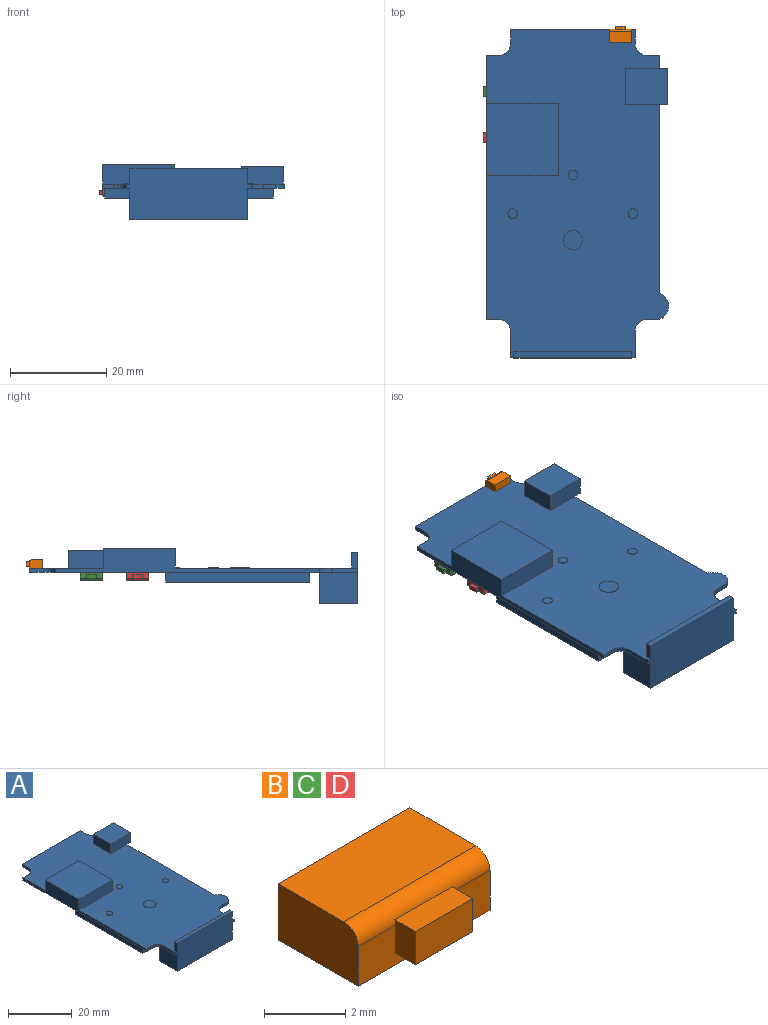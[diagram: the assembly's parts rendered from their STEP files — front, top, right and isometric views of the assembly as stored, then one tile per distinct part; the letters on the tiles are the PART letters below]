
ASSEMBLY  parts=4 mates=3
PART A: 54 faces, bbox 37.9x68.3x11.5 mm
  f0: plane 68.3x37.9mm, normal (0,0,1), area 2001.6mm2, adj f2,f3,f4,f5,f6,f7,f8,f9
  f1: plane 68.3x37.9mm, normal (0,0,-1), area 1085.4mm2, adj f2,f3,f4,f5,f6,f7,f8,f9
  f2: plane 49.4x0.9mm, normal (1,0,0), area 44.5mm2, adj f0,f1,f3,f18,f28
  f3: plane 2.5x0.9mm, normal (0,1,0), area 2.3mm2, adj f0,f1,f2,f4
  f4: cylinder r=2.5mm len=2.5mm, axis (0,0,-1), area 3.5mm2, adj f0,f1,f3,f5
  f5: plane 2.9x0.9mm, normal (1,0,0), area 2.6mm2, adj f0,f1,f4,f6
  f6: plane 25.9x0.9mm, normal (0,1,0), area 23.3mm2, adj f0,f1,f5,f7
  f7: plane 2.9x0.9mm, normal (-1,0,0), area 2.6mm2, adj f0,f1,f6,f8
  f8: cylinder r=2.5mm len=2.5mm, axis (0,0,-1), area 3.5mm2, adj f0,f1,f7,f9
  f9: plane 2.5x0.9mm, normal (0,1,0), area 2.3mm2, adj f0,f1,f8,f10
  f10: plane 54.9x5mm, normal (-1,0,0), area 110.5mm2, adj f0,f1,f9,f11,f19,f20,f22
  f11: plane 2.5x0.9mm, normal (0,-1,0), area 2.3mm2, adj f0,f1,f10,f12
  f12: cylinder r=2.5mm len=2.5mm, axis (0,0,-1), area 3.5mm2, adj f0,f1,f11,f13
  f13: plane 5.5x0.9mm, normal (-1,0,0), area 5mm2, adj f0,f1,f12,f14
  f14: plane 25.9x10.7mm, normal (0,-1,0), area 263.4mm2, adj f0,f1,f13,f15,f29,f31,f34,f46
  f15: plane 5.5x0.9mm, normal (1,0,0), area 5mm2, adj f0,f1,f14,f16
  f16: cylinder r=2.5mm len=2.5mm, axis (0,0,-1), area 3.5mm2, adj f0,f1,f15,f17
  f17: plane 2.5x0.9mm, normal (0,-1,0), area 2.3mm2, adj f0,f1,f16,f18
  f18: cylinder r=2.89mm len=5.5mm, axis (0,0,-1), area 6.5mm2, adj f0,f1,f2,f17
  f19: plane 14.9x4.1mm, normal (0,1,0), area 61.1mm2, adj f0,f10,f21,f22
  f20: plane 14.9x4.1mm, normal (0,-1,0), area 61.1mm2, adj f0,f10,f21,f22
  f21: plane 14.9x4.1mm, normal (1,0,0), area 61.1mm2, adj f0,f19,f20,f22
  f22: plane 14.9x14.9mm, normal (0,0,1), area 222mm2, adj f10,f19,f20,f21
  f23: plane 8.8x3.7mm, normal (0,1,0), area 32.6mm2, adj f0,f24,f26,f27,f28
  f24: plane 7.6x3.7mm, normal (-1,0,0), area 28.1mm2, adj f0,f23,f25,f27
  f25: plane 8.8x3.7mm, normal (0,-1,0), area 32.6mm2, adj f0,f24,f26,f27,f28
  f26: plane 7.6x3.7mm, normal (1,0,0), area 28.1mm2, adj f23,f25,f27,f28
  f27: plane 8.8x7.6mm, normal (0,0,1), area 66.9mm2, adj f23,f24,f25,f26
  f28: plane 7.6x1.7mm, normal (0,0,-1), area 12.9mm2, adj f2,f23,f25,f26
  f29: plane 8x6.5mm, normal (1,0,0), area 52mm2, adj f1,f14,f30,f34
  f30: plane 24.5x6.5mm, normal (0,1,0), area 159.3mm2, adj f1,f29,f31,f34
  f31: plane 8x6.5mm, normal (-1,0,0), area 52mm2, adj f1,f14,f30,f34
  f32: cylinder r=1mm len=6.5mm, axis (0,0,1), area 40.8mm2, adj f34,f36
  f33: cylinder r=1mm len=6.5mm, axis (0,0,1), area 40.8mm2, adj f34,f35
  f34: plane 24.5x8mm, normal (0,0,-1), area 189.7mm2, adj f14,f29,f30,f31,f32,f33
  f35: plane 2x2mm, normal (0,0,-1), area 3.1mm2, adj f33
  f36: plane 2x2mm, normal (0,0,-1), area 3.1mm2, adj f32
  f37: cylinder r=2mm len=4mm, axis (0,0,-1), area 1.3mm2, adj f0,f38
  f38: plane 4x4mm, normal (0,0,1), area 12.6mm2, adj f37
  f39: cylinder r=1mm len=2mm, axis (0,0,-1), area 0.6mm2, adj f0,f40
  f40: plane 2x2mm, normal (0,0,1), area 3.1mm2, adj f39
  f41: cylinder r=1mm len=2mm, axis (0,0,-1), area 0.6mm2, adj f0,f42
  f42: plane 2x2mm, normal (0,0,1), area 3.1mm2, adj f41
  f43: cylinder r=1mm len=2mm, axis (0,0,-1), area 0.6mm2, adj f0,f44
  f44: plane 2x2mm, normal (0,0,1), area 3.1mm2, adj f43
  f45: plane 24.5x3.3mm, normal (0,1,0), area 80.9mm2, adj f0,f46,f47,f48
  f46: plane 3.3x1.3mm, normal (-1,0,0), area 4.3mm2, adj f0,f14,f45,f48
  f47: plane 3.3x1.3mm, normal (1,0,0), area 4.3mm2, adj f0,f14,f45,f48
  f48: plane 24.5x1.3mm, normal (0,0,1), area 31.9mm2, adj f14,f45,f46,f47
  f49: plane 35x2mm, normal (0,-1,0), area 70mm2, adj f1,f50,f52,f53
  f50: plane 30x2mm, normal (-1,0,0), area 60mm2, adj f1,f49,f51,f53
  f51: plane 35x2mm, normal (0,1,0), area 70mm2, adj f1,f50,f52,f53
  f52: plane 30x2mm, normal (1,0,0), area 60mm2, adj f1,f49,f51,f53
  f53: plane 35x30mm, normal (0,0,-1), area 1050mm2, adj f49,f50,f51,f52
PART B: 12 faces, bbox 4.6x3.5x1.7 mm
  f0: plane 4.6x1.2mm, normal (0,-1,0), area 3.8mm2, adj f1,f3,f5,f6,f8,f9,f11
  f1: plane 2.8x1.7mm, normal (1,0,0), area 4.7mm2, adj f0,f2,f4,f5,f11
  f2: plane 4.6x1.7mm, normal (0,1,0), area 7.8mm2, adj f1,f3,f4,f5
  f3: plane 2.8x1.7mm, normal (-1,0,0), area 4.7mm2, adj f0,f2,f4,f5,f11
  f4: plane 4.6x2.3mm, normal (0,0,1), area 10.6mm2, adj f1,f2,f3,f11
  f5: plane 4.6x2.8mm, normal (0,0,-1), area 12.9mm2, adj f0,f1,f2,f3
  f6: plane 1x0.72mm, normal (1,0,0), area 0.7mm2, adj f0,f7,f9,f10,f11
  f7: plane 2x0.72mm, normal (0,0,1), area 1.4mm2, adj f6,f8,f10,f11
  f8: plane 1x0.72mm, normal (-1,0,0), area 0.7mm2, adj f0,f7,f9,f10,f11
  f9: plane 2x0.7mm, normal (0,0,-1), area 1.4mm2, adj f0,f6,f8,f10
  f10: plane 2x1mm, normal (0,-1,0), area 2mm2, adj f6,f7,f8,f9
  f11: cylinder r=0.5mm len=4.6mm, axis (-1,0,0), area 3.3mm2, adj f0,f1,f3,f4,f6,f7,f8
PART C: same geometry as B
PART D: same geometry as B
PLACE A t=(-12.95,-34.15,-0.9)mm
PLACE B rot(axis=(0,0,1),180deg) t=(-3.1,-1.4,0)mm
PLACE C rot(axis=(0.71,0.71,0),180deg) t=(-29.5,-12.9,-0.9)mm
PLACE D rot(axis=(0.71,0.71,0),180deg) t=(-29.5,-22.5,-0.9)mm
MATE fastened A.f0 <-> B.f5  axis (0,0,-1) through (0,0,0)mm
MATE fastened C.f5 <-> D.f5  axis (0,0,-1) through (-30.9,-20.2,-0.9)mm
MATE fastened A.f1 <-> C.f5  axis (0,0,1) through (-30.9,-10.6,-0.9)mm
